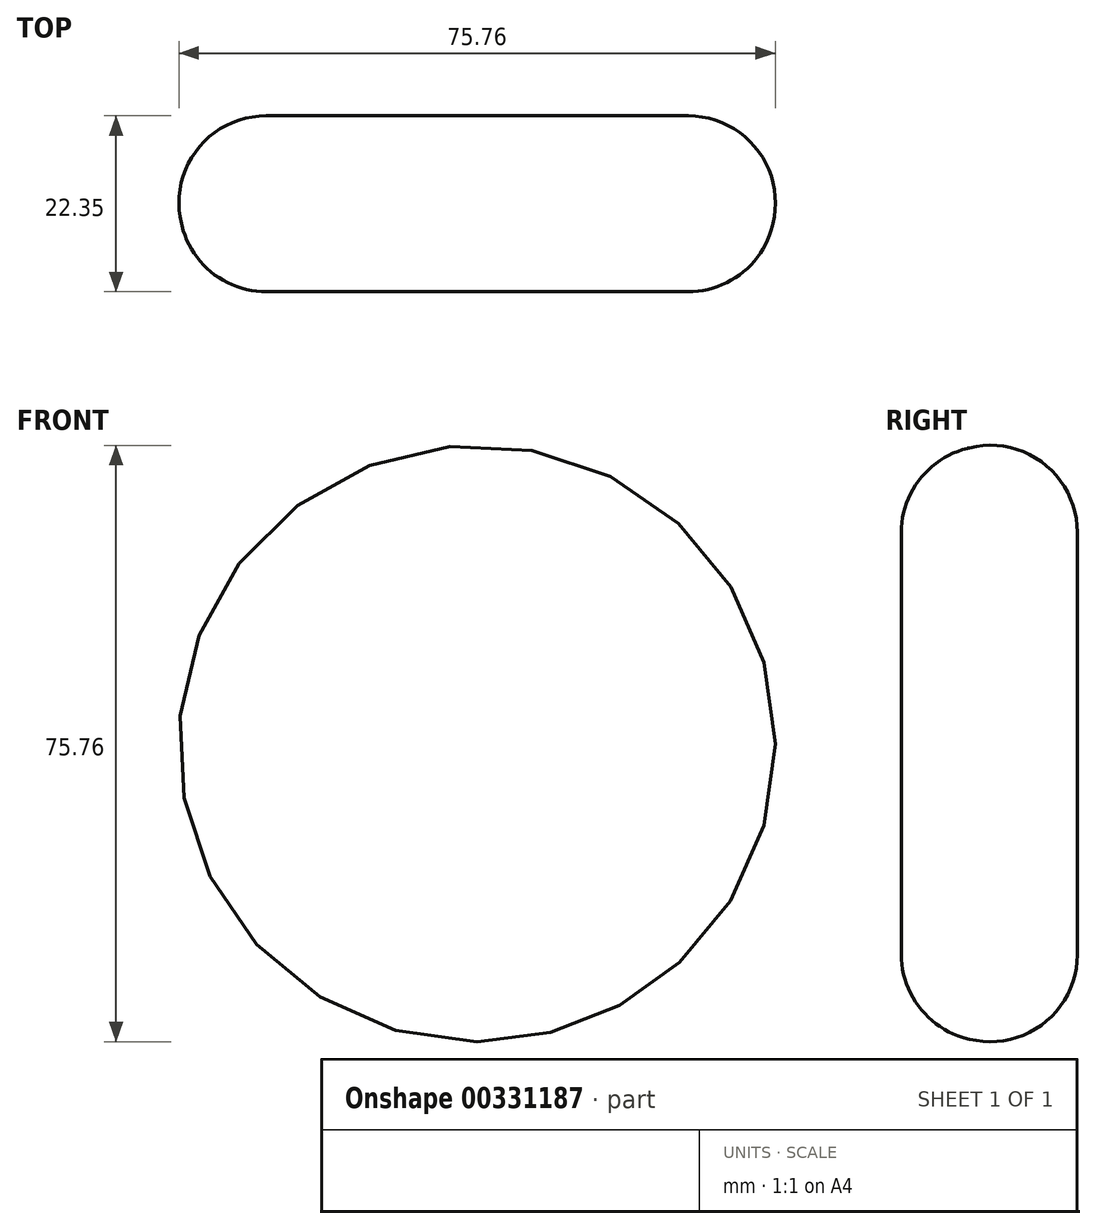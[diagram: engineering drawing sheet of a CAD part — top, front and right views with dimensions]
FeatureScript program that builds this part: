
annotation { "Feature Type Name" : "Feature", "Feature Type Description" : "" }
export const myFeature = defineFeature(function(context is Context, id is Id, definition is map)
    precondition{}
    {
        {
            var Q0;
            Q0=qCreatedBy(makeId("Front.planeOp"),FACE);
            var sketch = newSketch(context, id + "F0", { "sketchPlane" : qUnion([Q0])});
            skCircle(sketch, "E0", {"center": v(0, 0) * mm, "radius": 40.93 * mm});
            skSolve(sketch);
        }
        {
            var Q0;
            Q0=makeQuery(id+"F0.imprint","IMPRINT",FACE,{"disambiguationData":[TD([[makeQuery(id+"F0.imprint","IMPRINT",EDGE,{"derivedFrom":sQuery(id+"F0.wireOp",EDGE,"E0")}),1.0]])]});
            cPlane(context, id + "F1", {"entities" : qUnion([Q0]), "cplaneType" : CPlaneType.OFFSET, "offset" : 22.35 * mm, "width" : 152.4 * mm, "height" : 152.4 * mm});
        }
        {
            var Q0;
            Q0=qCreatedBy(id+"F1.planeOp",FACE);
            var sketch = newSketch(context, id + "F2", { "sketchPlane" : qUnion([Q0])});
            skCircle(sketch, "E1", {"center": v(0, 0) * mm, "radius": 35.43 * mm});
            skSolve(sketch);
        }
        {
            var Q0;
            Q0=makeQuery(id+"F0.imprint","IMPRINT",FACE,{"disambiguationData":[TD([[makeQuery(id+"F0.imprint","IMPRINT",EDGE,{"derivedFrom":sQuery(id+"F0.wireOp",EDGE,"E0")}),1.0]])]});
            var Q1;
            Q1=makeQuery(id+"F2.imprint","IMPRINT",FACE,{"disambiguationData":[TD([[makeQuery(id+"F2.imprint","IMPRINT",EDGE,{"derivedFrom":sQuery(id+"F2.wireOp",EDGE,"E1")}),1.0]])]});
            loft(context, id + "F3", {"sheetProfilesArray" : [{ "sheetProfileEntities" : qUnion([Q0]) }, { "sheetProfileEntities" : qUnion([Q1]) }]});
        }
        {
            var Q0;
            Q0=makeQuery(id+"F3.opLoft","MID_CAP_EDGE",EDGE,{"disambiguationData":[OSD([sQuery(id+"F0.wireOp",EDGE,"E0"),sQuery(id+"F2.wireOp",EDGE,"E1")])],"capPos":1.0});
            var Q1;
            Q1=makeQuery(id+"F3.opLoft","SWEPT_FACE",FACE,{"disambiguationData":[OSD([sQuery(id+"F0.wireOp",EDGE,"E0"),sQuery(id+"F2.wireOp",EDGE,"E1")])]});
            fillet(context, id + "F4", {"entities" : qUnion([Q0, Q1]), "radius" : 11.04 * mm, "tangentPropagation" : true, "allowEdgeOverflow" : false});
        }
    });
